# Revit family: Faucet-Lavatory-KOHLER-REFINED-K-23472T
name_source: partatom
category: Plumbing Fixtures
revit_build: Autodesk Revit 2017 (Build: 20160225_1515(x64)
units: mm (PartAtom-declared; Revit-internal decimal feet)

## family parameters
Cut with Voids When Loaded = No
Host = Face
OmniClass Number = 23.31.11.00
OmniClass Title = Faucets
Part Type = Normal
Room Calculation Point = No
Round Connector Dimension = Use Diameter
Shared = No

## types (4) — shared parameters
ADA Compliant = No
Assembly Code = D2010
CW Connection = Yes
Cold Water Inlet = Cold Water Inlet
Date Modified = 06/04/2020
Default Elevation = 36"
Description = Single handle basin faucet
Flow Rate = 0 GPM
HW Connection = Yes
Handle Clearance = 3 15/16"
Height = 6 1/8"
Hot Water Inlet = Hot Water Inlet
Length = 4 1/2"
Manufacturer = KOHLER Co.
Master Format 2014 = 22 41 39
Master Format 2014 Name = Residential Faucets, Supplies, and Trim
Material = Premium Metal Construction
Pressure = 0.00 psi
Product Name = REFINED
Spout Reach = 4 1/2"
URL = http://www.kohler.com.cn
Vent Connection = No
Waste Connection = No
Waste Water Outlet = Waste Water Outlet
WaterSense Certified = No
Width = 1 7/8"

## per-type parameters (varying)
| type | Drain Included | Finish | Lift Rod | Model | Product Documentation Link | Product Page URL | Type |
| With Drain, CP-Polished Chrome | Yes | Kohler-Metal-CP-Polished_Chrome | Yes | K-23472T-4-CP | http://files.kohler.com.cn | http://www.kohler.com.cn | 1 |
| With Drain, BN-Roman silver | Yes | Kohler-Metal-BN-Roman_Silver | Yes | K-23472T-4-BN | http://files.kohler.com.cn | http://www.kohler.com.cn | 2 |
| With Drain, RGD-Rose Gold | Yes | Kohler-Metal-RGD-Rose_Gold | Yes | K-23472T-4-RGD | http://files.kohler.com.cn | http://www.kohler.com.cn | 3 |
| Without Drain, CP-Polished Chrome | No | Kohler-Metal-CP-Polished_Chrome | No | K-23472T-4ND-CP |  |  | 4 |

## geometry (parser evidence)
native form markers: Sweep x5
no freeform markers — native parametric forms only
